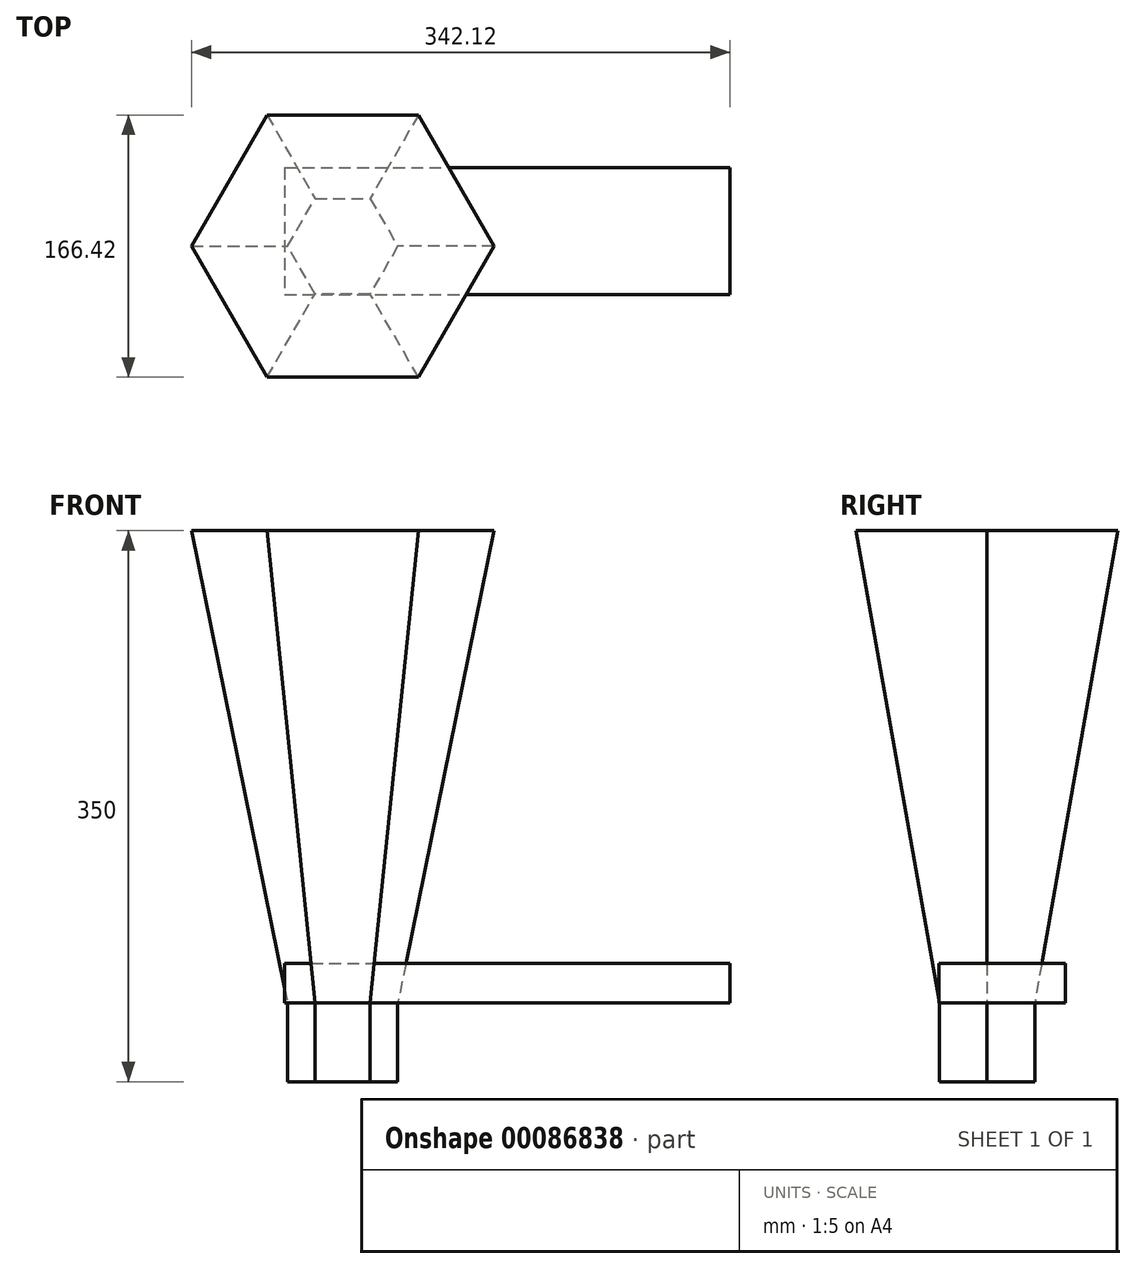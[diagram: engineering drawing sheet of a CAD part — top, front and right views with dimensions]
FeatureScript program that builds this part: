
annotation { "Feature Type Name" : "Feature", "Feature Type Description" : "" }
export const myFeature = defineFeature(function(context is Context, id is Id, definition is map)
    precondition{}
    {
        {
            var Q0;
            Q0=qCreatedBy(makeId("Top.planeOp"),FACE);
            var sketch = newSketch(context, id + "F0", { "sketchPlane" : qUnion([Q0])});
            skLineSegment(sketch, "E0.bottom", {"start": v(-55.09, -23.6) * mm, "end": v(44.91, -23.6) * mm});
            skLineSegment(sketch, "E0.top", {"start": v(-55.09, 20.91) * mm, "end": v(44.91, 20.91) * mm});
            skLineSegment(sketch, "E0.left", {"start": v(-55.09, -23.6) * mm, "end": v(-55.09, 20.91) * mm});
            skLineSegment(sketch, "E0.right", {"start": v(44.91, -23.6) * mm, "end": v(44.91, 20.91) * mm});
            skCircle(sketch, "E1.cCircle", {"center": v(-88.64, -63.83) * mm, "radius": 30.31 * mm, "construction": true});
            skLineSegment(sketch, "E1.0", {"start": v(-106.14, -33.52) * mm, "end": v(-71.14, -33.52) * mm});
            skLineSegment(sketch, "E1.1", {"start": v(-71.14, -33.52) * mm, "end": v(-53.64, -63.83) * mm});
            skLineSegment(sketch, "E1.2", {"start": v(-53.64, -63.83) * mm, "end": v(-71.14, -94.14) * mm});
            skLineSegment(sketch, "E1.3", {"start": v(-71.14, -94.14) * mm, "end": v(-106.14, -94.14) * mm});
            skLineSegment(sketch, "E1.4", {"start": v(-106.14, -94.14) * mm, "end": v(-123.64, -63.83) * mm});
            skLineSegment(sketch, "E1.5", {"start": v(-123.64, -63.83) * mm, "end": v(-106.14, -33.52) * mm});
            skPoint(sketch, "E1.0.midPoint", {"position": v(-88.64, -33.52) * mm});
            skSolve(sketch);
        }
        {
            var Q0;
            Q0=makeQuery(id+"F0.imprint","IMPRINT",FACE,{"disambiguationData":[TD([[makeQuery(id+"F0.imprint","IMPRINT",EDGE,{"derivedFrom":sQuery(id+"F0.wireOp",EDGE,"E1.0")}),-1.0]])]});
            extrude(context, id + "F1", {"entities" : qUnion([Q0]), "depth" : 300 * mm, "hasDraft" : true, "draftAngle" : 10 * degree, "hasSecondDirection" : true, "secondDirectionOppositeDirection" : true, "secondDirectionDepth" : 50 * mm});
        }
        {
            var Q0;
            Q0=qCreatedBy(makeId("Top.planeOp"),FACE);
            var sketch = newSketch(context, id + "F2", { "sketchPlane" : qUnion([Q0])});
            skLineSegment(sketch, "E2.bottom", {"start": v(-125.53, -14) * mm, "end": v(157.4, -14) * mm});
            skLineSegment(sketch, "E2.top", {"start": v(-125.53, -94.51) * mm, "end": v(157.4, -94.51) * mm});
            skLineSegment(sketch, "E2.left", {"start": v(-125.53, -14) * mm, "end": v(-125.53, -94.51) * mm});
            skLineSegment(sketch, "E2.right", {"start": v(157.4, -14) * mm, "end": v(157.4, -94.51) * mm});
            skLineSegment(sketch, "E3.bottom", {"start": v(-329.07, -29.4) * mm, "end": v(-299.55, -29.4) * mm});
            skLineSegment(sketch, "E3.top", {"start": v(-329.07, -65.29) * mm, "end": v(-299.55, -65.29) * mm});
            skLineSegment(sketch, "E3.left", {"start": v(-329.07, -29.4) * mm, "end": v(-329.07, -65.29) * mm});
            skLineSegment(sketch, "E3.right", {"start": v(-299.55, -29.4) * mm, "end": v(-299.55, -65.29) * mm});
            skSolve(sketch);
        }
        {
            var Q0;
            Q0=makeQuery(id+"F2.imprint","IMPRINT",FACE,{"disambiguationData":[TD([[makeQuery(id+"F2.imprint","IMPRINT",EDGE,{"derivedFrom":sQuery(id+"F2.wireOp",EDGE,"E2.bottom")}),-1.0]])]});
            extrude(context, id + "F3", {"entities" : qUnion([Q0]), "depth" : 25 * mm});
        }
    });
